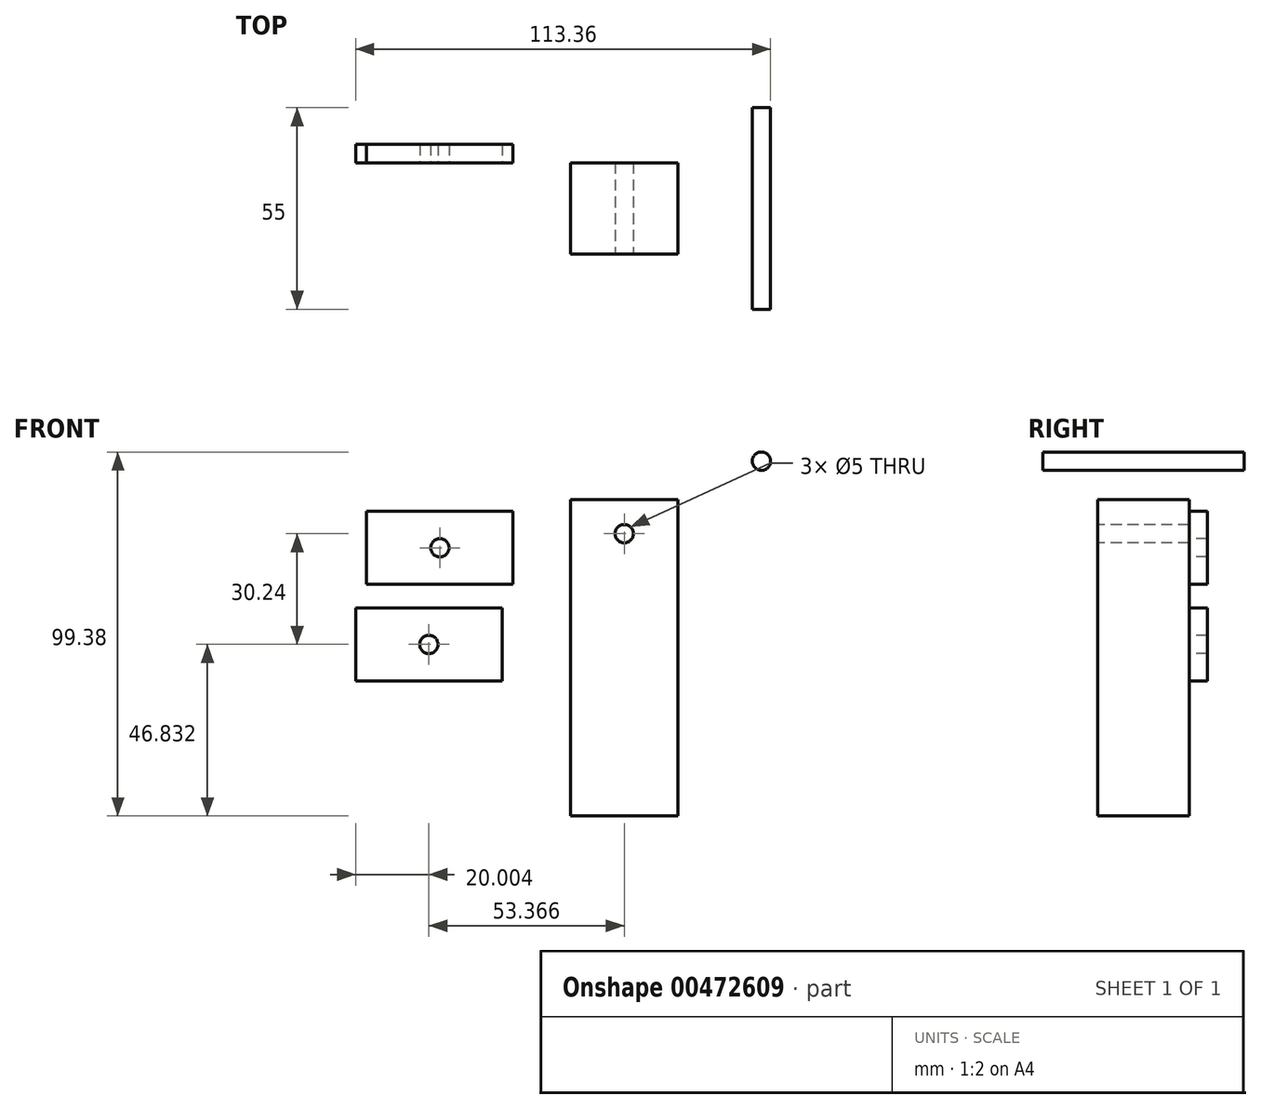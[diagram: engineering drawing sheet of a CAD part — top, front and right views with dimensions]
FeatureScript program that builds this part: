
annotation { "Feature Type Name" : "Feature", "Feature Type Description" : "" }
export const myFeature = defineFeature(function(context is Context, id is Id, definition is map)
    precondition{}
    {
        {
            var Q0;
            Q0=qCreatedBy(makeId("Front.planeOp"),FACE);
            var sketch = newSketch(context, id + "F0", { "sketchPlane" : qUnion([Q0])});
            skLineSegment(sketch, "E0.bottom", {"start": v(-14.72, 43.2) * mm, "end": v(14.72, 43.2) * mm});
            skLineSegment(sketch, "E0.top", {"start": v(-14.72, -43.2) * mm, "end": v(14.72, -43.2) * mm});
            skLineSegment(sketch, "E0.left", {"start": v(-14.72, 43.2) * mm, "end": v(-14.72, -43.2) * mm});
            skLineSegment(sketch, "E0.right", {"start": v(14.72, 43.2) * mm, "end": v(14.72, -43.2) * mm});
            skPoint(sketch, "E0.middle", {"position": v(0, 0) * mm});
            skSolve(sketch);
        }
        {
            var Q0;
            Q0=makeQuery(id+"F0.imprint","IMPRINT",FACE,{"disambiguationData":[TD([[makeQuery(id+"F0.imprint","IMPRINT",EDGE,{"derivedFrom":sQuery(id+"F0.wireOp",EDGE,"E0.bottom")}),-1.0]])]});
            extrude(context, id + "F1", {"entities" : qUnion([Q0]), "depth" : 25 * mm});
        }
        {
            var Q0;
            Q0=makeQuery(id+"F1.opExtrude","CAP_FACE",FACE,{"disambiguationData":[OSD([sQuery(id+"F0.wireOp",EDGE,"E0.bottom"),sQuery(id+"F0.wireOp",EDGE,"E0.top"),sQuery(id+"F0.wireOp",EDGE,"E0.left"),sQuery(id+"F0.wireOp",EDGE,"E0.right")])],"isStart":false});
            var sketch = newSketch(context, id + "F2", { "sketchPlane" : qUnion([Q0])});
            skCircle(sketch, "E1", {"center": v(0, 33.87) * mm, "radius": 2.5 * mm});
            skSolve(sketch);
        }
        {
            var Q0;
            Q0=sQuery(id+"F2.wireOp",VERTEX,"E1.center");
            var Q1;
            Q1=makeQuery(id+"F1.opExtrude","SWEPT_BODY",BODY,{"disambiguationData":[OSD([sQuery(id+"F0.wireOp",EDGE,"E0.bottom"),sQuery(id+"F0.wireOp",EDGE,"E0.top"),sQuery(id+"F0.wireOp",EDGE,"E0.left"),sQuery(id+"F0.wireOp",EDGE,"E0.right")])]});
            hole(context, id + "F3", {"style" : HoleStyle.SIMPLE, "endStyle" : HoleEndStyle.THROUGH, "holeDiameter" : 5 * mm, "isTappedThrough" : true, "tappedDepth" : 12 * mm, "tapClearance" : 3, "locations" : qUnion([Q0]), "scope" : qUnion([Q1])});
        }
        {
            var Q0;
            Q0=qCreatedBy(makeId("Front.planeOp"),FACE);
            var sketch = newSketch(context, id + "F4", { "sketchPlane" : qUnion([Q0])});
            skCircle(sketch, "E2", {"center": v(37.5, 53.68) * mm, "radius": 2.5 * mm});
            skSolve(sketch);
        }
        {
            var Q0;
            Q0=makeQuery(id+"F4.imprint","IMPRINT",FACE,{"disambiguationData":[TD([[makeQuery(id+"F4.imprint","IMPRINT",EDGE,{"derivedFrom":sQuery(id+"F4.wireOp",EDGE,"E2")}),1.0]])]});
            extrude(context, id + "F5", {"entities" : qUnion([Q0]), "depth" : 40 * mm, "hasSecondDirection" : true, "secondDirectionOppositeDirection" : true, "secondDirectionDepth" : 15 * mm});
        }
        {
            var Q0;
            Q0=qCreatedBy(makeId("Front.planeOp"),FACE);
            var sketch = newSketch(context, id + "F6", { "sketchPlane" : qUnion([Q0])});
            skLineSegment(sketch, "E3.bottom", {"start": v(-70.36, 40) * mm, "end": v(-30.36, 40) * mm});
            skLineSegment(sketch, "E3.top", {"start": v(-70.36, 20) * mm, "end": v(-30.36, 20) * mm});
            skLineSegment(sketch, "E3.left", {"start": v(-70.36, 40) * mm, "end": v(-70.36, 20) * mm});
            skLineSegment(sketch, "E3.right", {"start": v(-30.36, 40) * mm, "end": v(-30.36, 20) * mm});
            skCircle(sketch, "E4", {"center": v(-50.36, 30) * mm, "radius": 2.5 * mm});
            skPoint(sketch, "E4.centerSnap0", {"position": v(-50.36, 20) * mm});
            skSolve(sketch);
        }
        {
            var Q0;
            Q0=makeQuery(id+"F6.imprint","IMPRINT",FACE,{"disambiguationData":[TD([[makeQuery(id+"F6.imprint","IMPRINT",EDGE,{"derivedFrom":sQuery(id+"F6.wireOp",EDGE,"E3.bottom")}),-1.0]])]});
            extrude(context, id + "F7", {"entities" : qUnion([Q0]), "oppositeDirection" : true, "depth" : 5 * mm});
        }
        {
            var Q0;
            Q0=qCreatedBy(makeId("Front.planeOp"),FACE);
            var sketch = newSketch(context, id + "F8", { "sketchPlane" : qUnion([Q0])});
            skLineSegment(sketch, "E5.bottom", {"start": v(-73.37, 13.63) * mm, "end": v(-33.37, 13.63) * mm});
            skLineSegment(sketch, "E5.top", {"start": v(-73.37, -6.37) * mm, "end": v(-33.37, -6.37) * mm});
            skLineSegment(sketch, "E5.left", {"start": v(-73.37, 13.63) * mm, "end": v(-73.37, -6.37) * mm});
            skLineSegment(sketch, "E5.right", {"start": v(-33.37, 13.63) * mm, "end": v(-33.37, -6.37) * mm});
            skCircle(sketch, "E6", {"center": v(-53.37, 3.63) * mm, "radius": 2.5 * mm});
            skSolve(sketch);
        }
        {
            var Q0;
            Q0=makeQuery(id+"F8.imprint","IMPRINT",FACE,{"disambiguationData":[TD([[makeQuery(id+"F8.imprint","IMPRINT",EDGE,{"derivedFrom":sQuery(id+"F8.wireOp",EDGE,"E5.bottom")}),-1.0]])]});
            extrude(context, id + "F9", {"entities" : qUnion([Q0]), "oppositeDirection" : true, "depth" : 5 * mm});
        }
    });
